# Revit family: Pressure_Reducing_Valves-Acorn-Controls-RV03P0_Series
name_source: partatom
category: Pipe Accessories
units: mm (PartAtom-declared; Revit-internal decimal feet)

## family parameters
Always vertical = Yes
Cut with Voids When Loaded = No
OmniClass Number = 23.65.55.14.17
OmniClass Title = Adjusting/Controlling Valves for Liquid Services
Part Type = Valve - Breaks Into
Round Connector Dimension = Use Diameter
Shared = No
Work Plane-Based = No

## types (6) — shared parameters
Adjustable Pressure Range = 10-75 PSI (69-517 kPa)
Assembly Code = D2090900
Body Material = Metal-Acorn-Lead Free Brass
Bonnet Material = Metal-Acorn-UV Resistant Material
Description = Pressure Reducing Valves
Factory Preset = 50±5 PSI (345kPa)
IAPMO Compliance = Comply with the national lead-free law, ASSE 1003 & NSF-61.
Manufacturer = Acorn
P0 Plastic = Yes
PH Plastic HP - High Pressure Spring = No
Pressure Rating = 400 PSI (2758 kPa)
S0 Steel = No
SH Steel HP - High Pressure Spring = No
Temperature Rating = 180°F (82.2°C)
URL = https://www.acorneng.com
cUPC Compliant = Yes

## per-type parameters (varying)
| type | A Dimension | Connection Inlet Description | Connection Outlet Description | D Dimension | E Dimension | Valve Size |
| RV03P0-1000 | 3 3/8" | 1/2" Inlet Connection | 1/2" Outlet Connection | 1 5/8" | 4 3/4" | 1/2" |
| RV03P0-2000 | 3 3/8" | 3/4" Inlet Connection | 3/4" Outlet Connection | 1 5/8" | 4 3/4" | 3/4" |
| RV03P0-3000 | 3 7/8" | 1" Inlet Connection | 1" Outlet Connection | 1 7/8" | 5 1/2" | 1" |
| RV03P0-4000 | 5" | 1 1/4" Inlet Connection | 1 1/4" Outlet Connection | 2 3/8" | 8 1/8" | 1 1/4" |
| RV03P0-5000 | 5" | 1 1/2" Inlet Connection | 1 1/2" Outlet Connection | 2 7/8" | 8 1/8" | 1 1/2" |
| RV03P0-6000 | 5" | 2 Inlet Connection | 2 Outlet Connection | 3 1/2" | 8 1/8" | 2" |

note: column(s) folded — value = type name in every type: Model

## geometry (parser evidence)
native form markers: Sweep x3
no freeform markers — native parametric forms only
